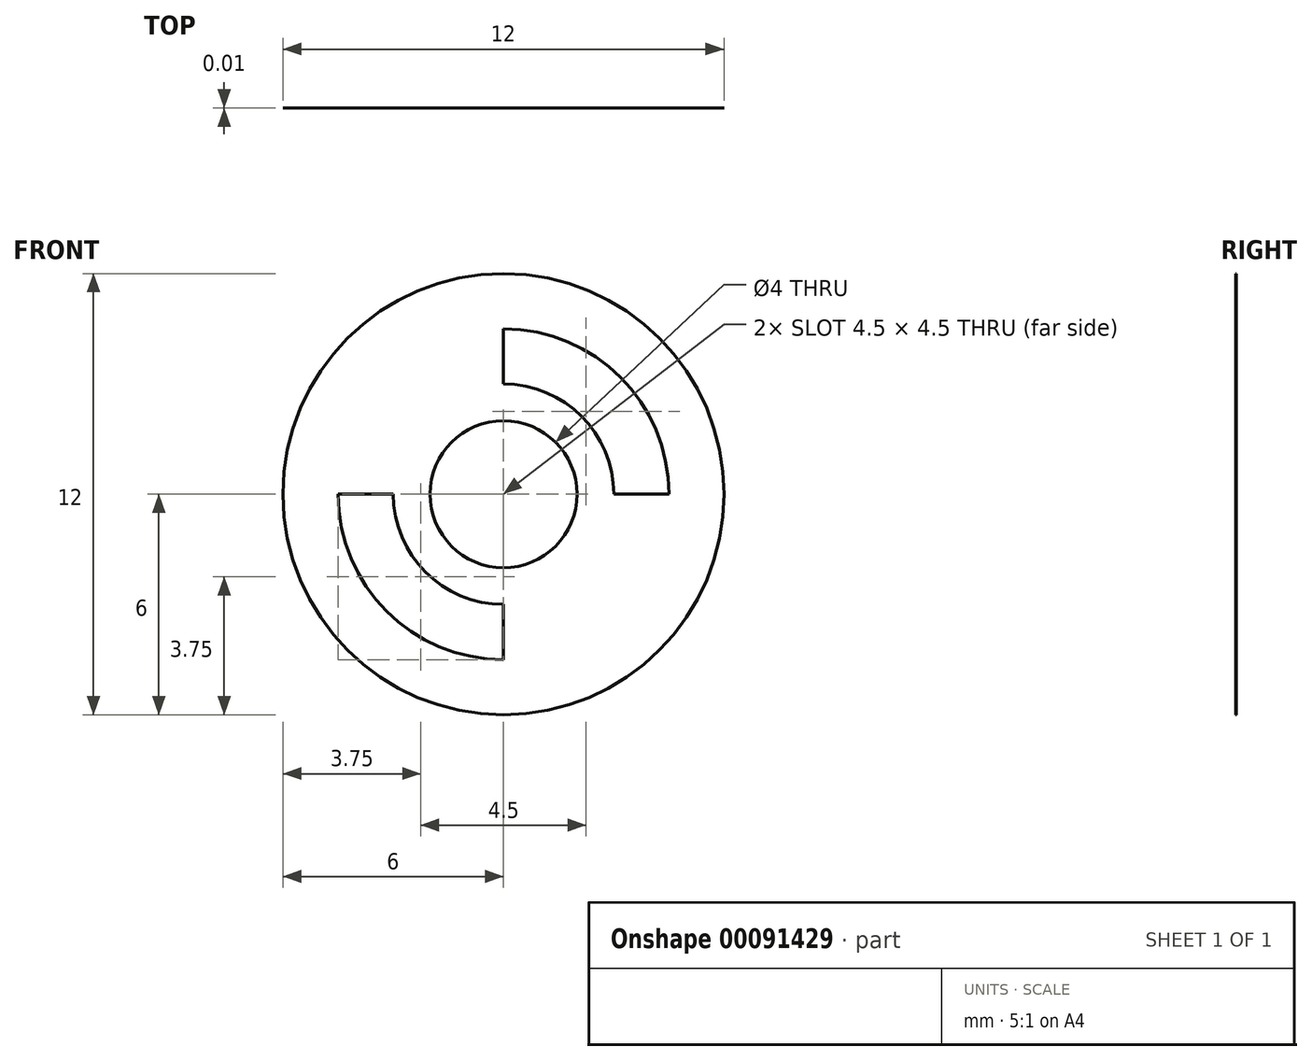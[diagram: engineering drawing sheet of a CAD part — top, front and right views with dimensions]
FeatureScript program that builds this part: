
annotation { "Feature Type Name" : "Feature", "Feature Type Description" : "" }
export const myFeature = defineFeature(function(context is Context, id is Id, definition is map)
    precondition{}
    {
        {
            var Q0;
            Q0=qCreatedBy(makeId("Front.planeOp"),FACE);
            var sketch = newSketch(context, id + "F0", { "sketchPlane" : qUnion([Q0])});
            skCircle(sketch, "E0", {"center": v(0, 0) * mm, "radius": 6 * mm});
            skCircle(sketch, "E1", {"center": v(0, 0) * mm, "radius": 2 * mm});
            skCircle(sketch, "E2", {"center": v(0, 0) * mm, "radius": 4.5 * mm});
            skCircle(sketch, "E3", {"center": v(0, 0) * mm, "radius": 3 * mm});
            skLineSegment(sketch, "E4", {"start": v(0, -3) * mm, "end": v(0, -4.5) * mm});
            skLineSegment(sketch, "E5", {"start": v(-3, 0) * mm, "end": v(-4.5, 0) * mm});
            skLineSegment(sketch, "E6", {"start": v(0, 3) * mm, "end": v(0, 4.5) * mm});
            skLineSegment(sketch, "E7", {"start": v(3, 0) * mm, "end": v(4.5, 0) * mm});
            skSolve(sketch);
        }
        {
            var Q0;
            Q0 = qSketchRegion(id + "F0", true);
            var Q1;
            {var subQ0=sQuery(id+"F0.wireOp",EDGE,"E4");Q1=makeQuery(id+"F0.imprint","IMPRINT",FACE,{"disambiguationData":[TD([[makeQuery(id+"F0.imprint","IMPRINT",EDGE,{"derivedFrom":subQ0}),1.0]])]});}
            var Q2;
            Q2=makeQuery(id+"F0.imprint","IMPRINT",FACE,{"disambiguationData":[TD([[makeQuery(id+"F0.imprint","IMPRINT",EDGE,{"derivedFrom":sQuery(id+"F0.wireOp",EDGE,"E1")}),-1.0]])]});
            var Q3;
            {var subQ0=sQuery(id+"F0.wireOp",EDGE,"E5");Q3=makeQuery(id+"F0.imprint","IMPRINT",FACE,{"disambiguationData":[TD([[makeQuery(id+"F0.imprint","IMPRINT",EDGE,{"derivedFrom":subQ0}),-1.0]])]});}
            extrude(context, id + "F1", {"entities" : qUnion([Q0, Q1, Q2, Q3]), "depth" : 1 / 101.6 * mm});
        }
    });
